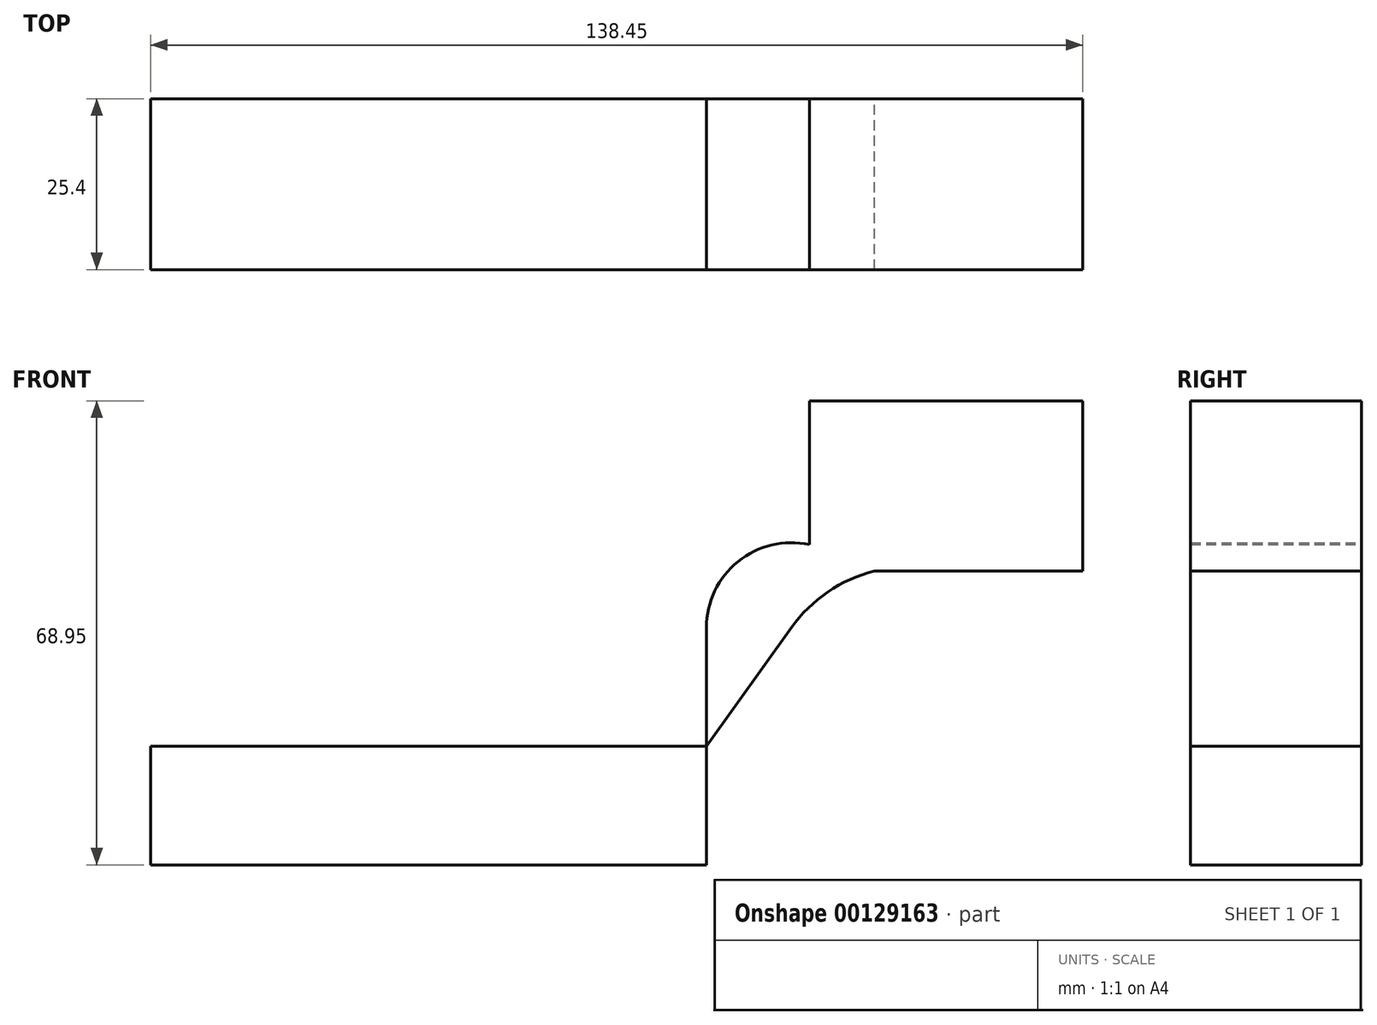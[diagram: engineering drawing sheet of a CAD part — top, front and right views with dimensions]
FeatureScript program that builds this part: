
annotation { "Feature Type Name" : "Feature", "Feature Type Description" : "" }
export const myFeature = defineFeature(function(context is Context, id is Id, definition is map)
    precondition{}
    {
        {
            var Q0;
            Q0=qCreatedBy(makeId("Front.planeOp"),FACE);
            var sketch = newSketch(context, id + "F0", { "sketchPlane" : qUnion([Q0])});
            skLineSegment(sketch, "E0.bottom", {"start": v(-41.28, 8.82) * mm, "end": v(41.28, 8.82) * mm});
            skLineSegment(sketch, "E0.top", {"start": v(-41.28, -8.82) * mm, "end": v(41.28, -8.82) * mm});
            skLineSegment(sketch, "E0.left", {"start": v(-41.28, 8.82) * mm, "end": v(-41.28, -8.82) * mm});
            skLineSegment(sketch, "E0.right", {"start": v(41.28, 8.82) * mm, "end": v(41.28, -8.82) * mm});
            skPoint(sketch, "E0.middle", {"position": v(0, 0) * mm});
            skLineSegment(sketch, "E1.bottom", {"start": v(97.18, 60.13) * mm, "end": v(56.55, 60.13) * mm});
            skLineSegment(sketch, "E1.top", {"start": v(97.18, 34.84) * mm, "end": v(56.55, 34.84) * mm});
            skLineSegment(sketch, "E1.left", {"start": v(97.18, 60.13) * mm, "end": v(97.18, 34.84) * mm});
            skLineSegment(sketch, "E1.right", {"start": v(56.55, 60.13) * mm, "end": v(56.55, 34.84) * mm});
            skPoint(sketch, "E1.middle", {"position": v(76.87, 47.49) * mm});
            skLineSegment(sketch, "E2", {"start": v(41.28, 8.82) * mm, "end": v(41.28, 26.44) * mm});
            skArc(sketch, "E3", {"start": v(41.28, 26.44) * mm, "mid": v(46.02, 36.3) * mm, "end": v(56.69, 38.73) * mm});
            skLineSegment(sketch, "E4", {"start": v(56.69, 38.73) * mm, "end": v(76.87, 38.73) * mm});
            skPoint(sketch, "E4.endSnap0", {"position": v(76.87, 34.84) * mm});
            skLineSegment(sketch, "E5", {"start": v(41.28, 8.82) * mm, "end": v(53.89, 26.44) * mm});
            skArc(sketch, "E6", {"start": v(53.89, 26.44) * mm, "mid": v(64.08, 34.19) * mm, "end": v(76.87, 34.84) * mm});
            skLineSegment(sketch, "E7.bottom", {"start": v(56.69, 38.73) * mm, "end": v(97.18, 38.73) * mm});
            skLineSegment(sketch, "E7.top", {"start": v(56.69, 60.13) * mm, "end": v(97.18, 60.13) * mm});
            skLineSegment(sketch, "E7.left", {"start": v(56.69, 38.73) * mm, "end": v(56.69, 60.13) * mm});
            skLineSegment(sketch, "E7.right", {"start": v(97.18, 38.73) * mm, "end": v(97.18, 60.13) * mm});
            skLineSegment(sketch, "E8", {"start": v(76.87, 38.73) * mm, "end": v(76.87, 34.84) * mm});
            skLineSegment(sketch, "E9", {"start": v(97.18, 38.73) * mm, "end": v(97.18, 34.84) * mm});
            skSolve(sketch);
        }
        {
            var Q0;
            Q0 = qSketchRegion(id + "F0", true);
            extrude(context, id + "F1", {"entities" : qUnion([Q0]), "endBound" : BoundingType.SYMMETRIC, "depth" : 25.4 * mm});
        }
    });
